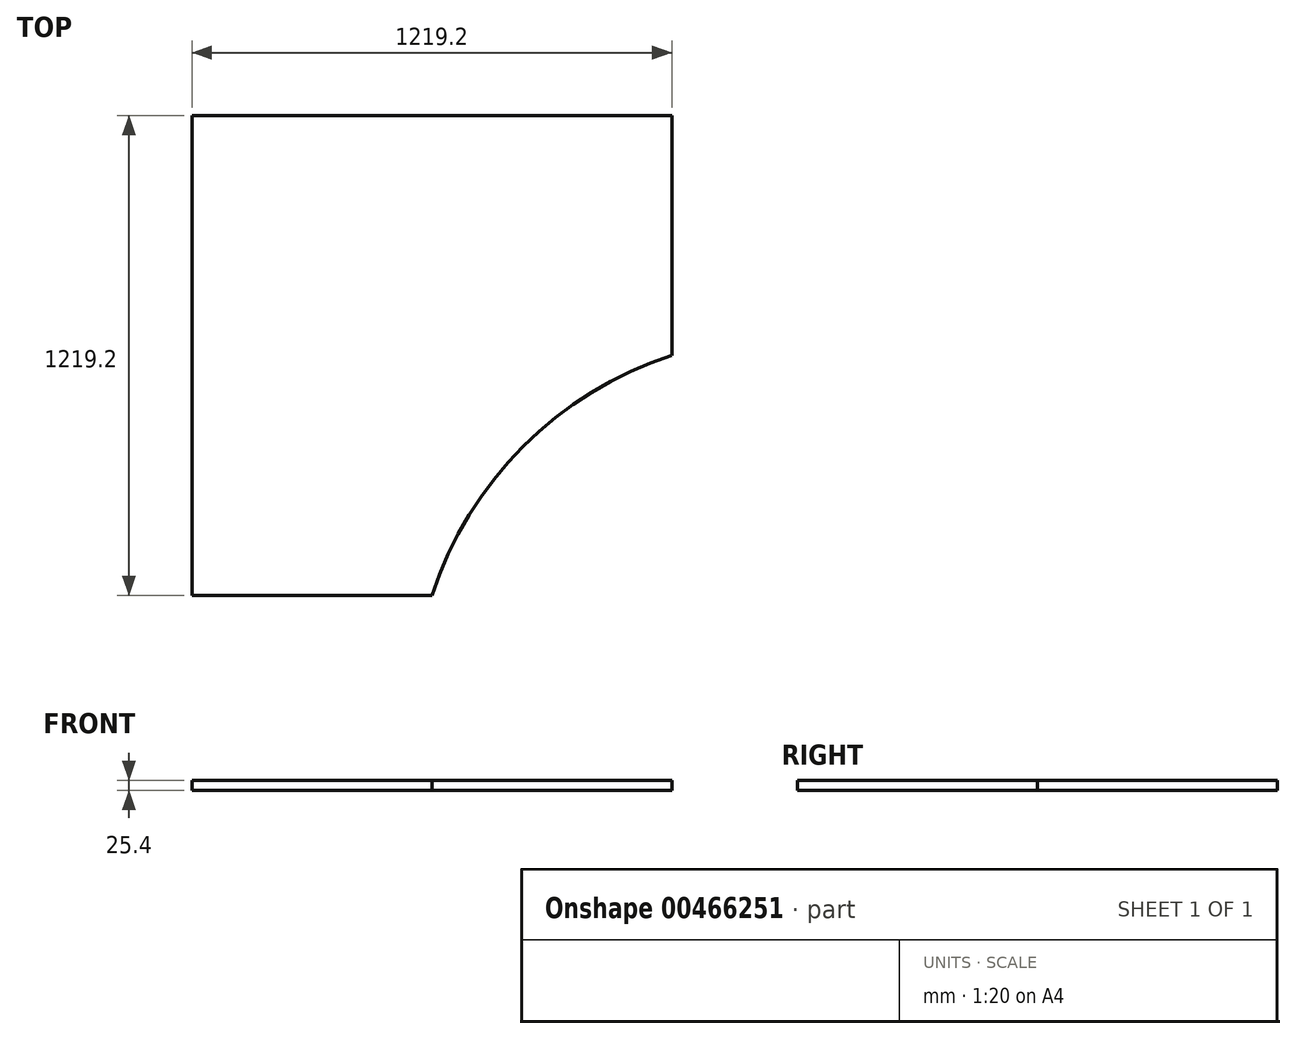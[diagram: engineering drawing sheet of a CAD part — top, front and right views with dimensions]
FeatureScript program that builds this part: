
annotation { "Feature Type Name" : "Feature", "Feature Type Description" : "" }
export const myFeature = defineFeature(function(context is Context, id is Id, definition is map)
    precondition{}
    {
        {
            var Q0;
            Q0=qCreatedBy(makeId("Top.planeOp"),FACE);
            var sketch = newSketch(context, id + "F0", { "sketchPlane" : qUnion([Q0])});
            skLineSegment(sketch, "E0.bottom", {"start": v(-1621.7, 2408.2) * mm, "end": v(1527.9, 2408.2) * mm});
            skLineSegment(sketch, "E0.top", {"start": v(-1621.7, -868.4) * mm, "end": v(1527.9, -868.4) * mm});
            skLineSegment(sketch, "E0.left", {"start": v(-1621.7, 2408.2) * mm, "end": v(-1621.7, -868.4) * mm});
            skLineSegment(sketch, "E0.right", {"start": v(1527.9, 2408.2) * mm, "end": v(1527.9, -868.4) * mm});
            skLineSegment(sketch, "E1.bottom", {"start": v(-1342.3, -868.4) * mm, "end": v(-529.5, -868.4) * mm});
            skLineSegment(sketch, "E1.top", {"start": v(-1342.3, -978.05) * mm, "end": v(-529.5, -978.05) * mm});
            skLineSegment(sketch, "E1.left", {"start": v(-1342.3, -868.4) * mm, "end": v(-1342.3, -978.05) * mm});
            skLineSegment(sketch, "E1.right", {"start": v(-529.5, -868.4) * mm, "end": v(-529.5, -978.05) * mm});
            skSolve(sketch);
        }
        {
            var Q0;
            Q0=qCreatedBy(makeId("Top.planeOp"),FACE);
            var sketch = newSketch(context, id + "F1", { "sketchPlane" : qUnion([Q0])});
            skLineSegment(sketch, "E2.bottom", {"start": v(-1621.7, 2408.2) * mm, "end": v(-402.5, 2408.2) * mm});
            skLineSegment(sketch, "E2.top", {"start": v(-1621.7, 1189) * mm, "end": v(-402.5, 1189) * mm});
            skLineSegment(sketch, "E2.left", {"start": v(-1621.7, 2408.2) * mm, "end": v(-1621.7, 1189) * mm});
            skLineSegment(sketch, "E2.right", {"start": v(-402.5, 2408.2) * mm, "end": v(-402.5, 1189) * mm});
            skCircle(sketch, "E3", {"center": v(-106.69, 893.2) * mm, "radius": 952.5 * mm});
            skLineSegment(sketch, "E4", {"start": v(-106.69, 893.2) * mm, "end": v(-402.5, 1189) * mm});
            skPoint(sketch, "E5", {"position": v(-1012.1, 1189) * mm});
            skSolve(sketch);
        }
        {
            var Q0;
            {var subQ1=sQuery(id+"F1.wireOp",EDGE,"E2.bottom");Q0=makeQuery(id+"F1.imprint","IMPRINT",FACE,{"disambiguationData":[TD([[makeQuery(id+"F1.imprint","IMPRINT",EDGE,{"derivedFrom":subQ1}),-1.0]])]});}
            extrude(context, id + "F2", {"entities" : qUnion([Q0]), "depth" : 25.4 * mm});
        }
    });
